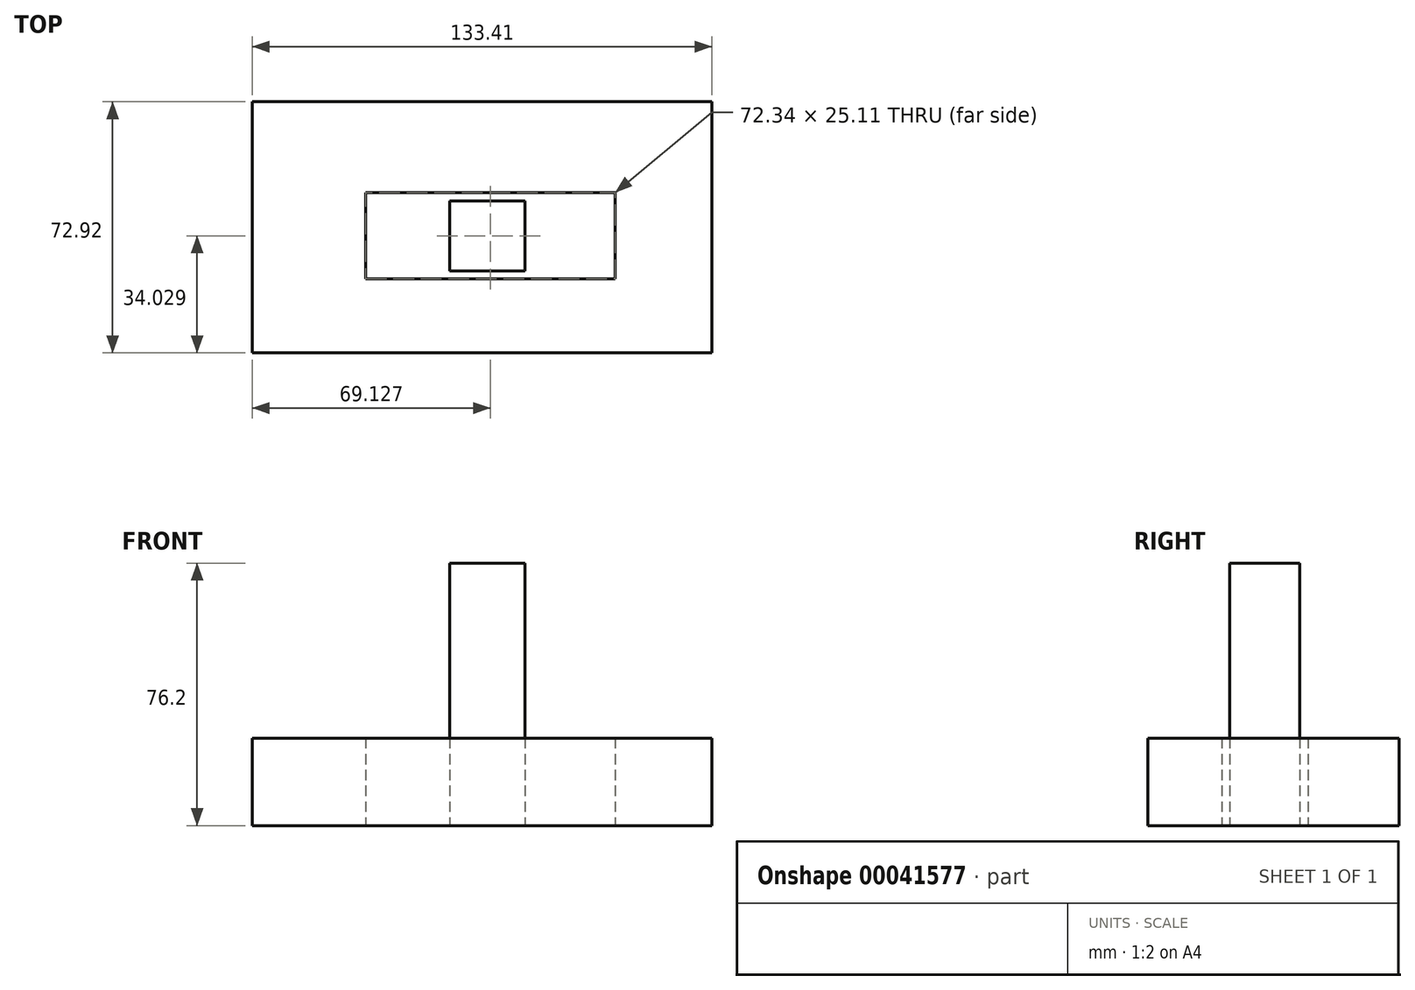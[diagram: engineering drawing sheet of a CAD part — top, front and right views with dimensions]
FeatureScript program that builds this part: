
annotation { "Feature Type Name" : "Feature", "Feature Type Description" : "" }
export const myFeature = defineFeature(function(context is Context, id is Id, definition is map)
    precondition{}
    {
        {
            var Q0;
            Q0=qCreatedBy(makeId("Top.planeOp"),FACE);
            var sketch = newSketch(context, id + "F0", { "sketchPlane" : qUnion([Q0])});
            skLineSegment(sketch, "E0.bottom", {"start": v(26.2, 21.48) * mm, "end": v(-46.14, 21.48) * mm});
            skLineSegment(sketch, "E0.top", {"start": v(26.2, 46.58) * mm, "end": v(-46.14, 46.58) * mm});
            skLineSegment(sketch, "E0.left", {"start": v(26.2, 21.48) * mm, "end": v(26.2, 46.58) * mm});
            skLineSegment(sketch, "E0.right", {"start": v(-46.14, 21.48) * mm, "end": v(-46.14, 46.58) * mm});
            skLineSegment(sketch, "E1.bottom", {"start": v(54.3, 0) * mm, "end": v(-79.1, 0) * mm});
            skLineSegment(sketch, "E1.top", {"start": v(54.3, 72.92) * mm, "end": v(-79.1, 72.92) * mm});
            skLineSegment(sketch, "E1.left", {"start": v(54.3, 0) * mm, "end": v(54.3, 72.92) * mm});
            skLineSegment(sketch, "E1.right", {"start": v(-79.1, 0) * mm, "end": v(-79.1, 72.92) * mm});
            skSolve(sketch);
        }
        {
            var Q0;
            Q0=makeQuery(id+"F0.imprint","IMPRINT",FACE,{"disambiguationData":[TD([[makeQuery(id+"F0.imprint","IMPRINT",EDGE,{"derivedFrom":sQuery(id+"F0.wireOp",EDGE,"E0.bottom")}),1.0]])]});
            extrude(context, id + "F1", {"entities" : qUnion([Q0]), "depth" : 25.4 * mm});
        }
        {
            var Q0;
            Q0=qCreatedBy(makeId("Top.planeOp"),FACE);
            var sketch = newSketch(context, id + "F2", { "sketchPlane" : qUnion([Q0])});
            skLineSegment(sketch, "E2.bottom", {"start": v(-21.77, 44.1) * mm, "end": v(0, 44.1) * mm});
            skLineSegment(sketch, "E2.top", {"start": v(-21.77, 23.84) * mm, "end": v(0, 23.84) * mm});
            skLineSegment(sketch, "E2.left", {"start": v(-21.77, 44.1) * mm, "end": v(-21.77, 23.84) * mm});
            skLineSegment(sketch, "E2.right", {"start": v(0, 44.1) * mm, "end": v(0, 23.84) * mm});
            skSolve(sketch);
        }
        {
            var Q0;
            Q0=makeQuery(id+"F2.imprint","IMPRINT",FACE,{"disambiguationData":[TD([[makeQuery(id+"F2.imprint","IMPRINT",EDGE,{"derivedFrom":sQuery(id+"F2.wireOp",EDGE,"E2.bottom")}),-1.0]])]});
            extrude(context, id + "F3", {"entities" : qUnion([Q0]), "depth" : 76.2 * mm});
        }
    });
